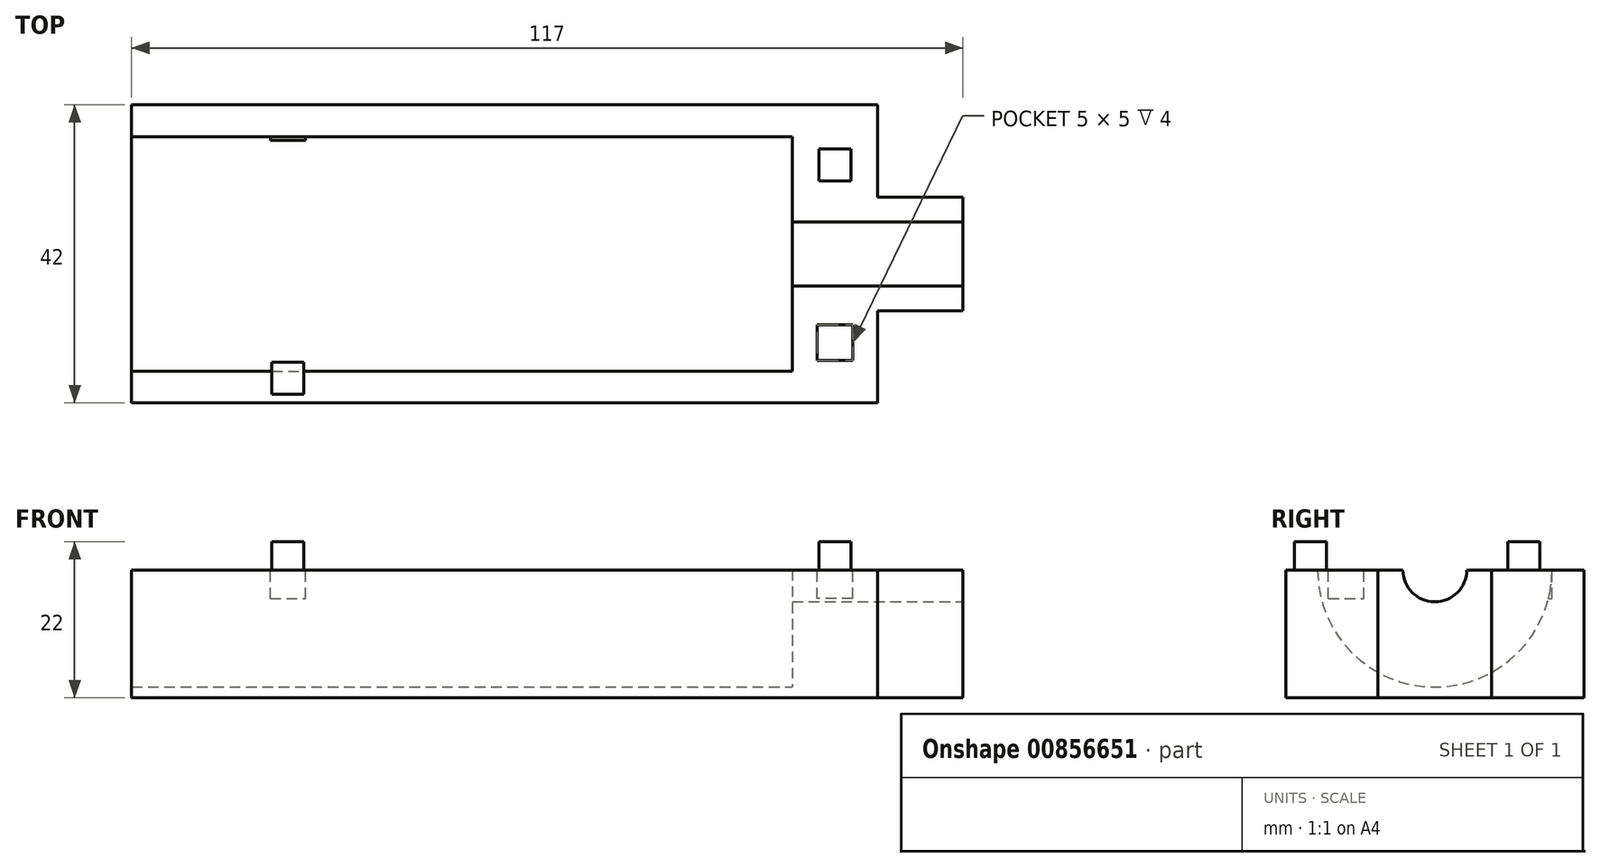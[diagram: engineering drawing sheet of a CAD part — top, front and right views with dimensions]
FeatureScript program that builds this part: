
annotation { "Feature Type Name" : "Feature", "Feature Type Description" : "" }
export const myFeature = defineFeature(function(context is Context, id is Id, definition is map)
    precondition{}
    {
        {
            var Q0;
            Q0=qCreatedBy(makeId("Top.planeOp"),FACE);
            var sketch = newSketch(context, id + "F0", { "sketchPlane" : qUnion([Q0])});
            skLineSegment(sketch, "E0.bottom", {"start": v(40, -21) * mm, "end": v(-40, -21) * mm});
            skLineSegment(sketch, "E0.top", {"start": v(40, 21) * mm, "end": v(-40, 21) * mm});
            skLineSegment(sketch, "E0.left", {"start": v(40, -21) * mm, "end": v(40, 21) * mm});
            skLineSegment(sketch, "E0.right", {"start": v(-40, -21) * mm, "end": v(-40, 21) * mm});
            skPoint(sketch, "E0.middle", {"position": v(0, 0) * mm});
            skSolve(sketch);
        }
        {
            var Q0;
            Q0 = qSketchRegion(id + "F0", true);
            extrude(context, id + "F1", {"entities" : qUnion([Q0]), "depth" : 22 * mm, "offsetDistance" : 25 * mm});
        }
        {
            var Q0;
            Q0=makeQuery(id+"F1.opExtrude","SWEPT_FACE",FACE,{"disambiguationData":[OSD([sQuery(id+"F0.wireOp",EDGE,"E0.left")])]});
            var sketch = newSketch(context, id + "F2", { "sketchPlane" : qUnion([Q0])});
            skCircle(sketch, "E1", {"center": v(0, 22) * mm, "radius": 16.5 * mm});
            skCircle(sketch, "E2", {"center": v(0, 22) * mm, "radius": 14 * mm});
            skCircle(sketch, "E3", {"center": v(0, 22) * mm, "radius": 4.5 * mm});
            skSolve(sketch);
        }
        {
            var Q0;
            {var subQ0=sQuery(id+"F2.wireOp",EDGE,"E1");var subQ1=makeQuery(id+"F1.opExtrude","CAP_EDGE",EDGE,{"disambiguationData":[OSD([sQuery(id+"F0.wireOp",EDGE,"E0.left")])],"isStart":false});var subQ2=makeQuery(id+"F2.imprint","INTERSECT",VERTEX,{"disambiguationData":[OD(0.0)],"derivedFrom":[subQ1,subQ0]});Q0=makeQuery(id+"F2.imprint","IMPRINT",FACE,{"disambiguationData":[TD([[makeQuery(id+"F2.imprint","IMPRINT",EDGE,{"disambiguationData":[TD([[subQ2,-1.0]])],"derivedFrom":subQ0}),1.0]])]});}
            var Q1;
            {var subQ0=sQuery(id+"F2.wireOp",EDGE,"E2");var subQ1=makeQuery(id+"F1.opExtrude","CAP_EDGE",EDGE,{"disambiguationData":[OSD([sQuery(id+"F0.wireOp",EDGE,"E0.left")])],"isStart":false});var subQ2=makeQuery(id+"F2.imprint","INTERSECT",VERTEX,{"disambiguationData":[OD(0.0)],"derivedFrom":[subQ1,subQ0]});Q1=makeQuery(id+"F2.imprint","IMPRINT",FACE,{"disambiguationData":[TD([[makeQuery(id+"F2.imprint","IMPRINT",EDGE,{"disambiguationData":[TD([[subQ2,-1.0]])],"derivedFrom":subQ0}),1.0]])]});}
            var Q2;
            {var subQ0=sQuery(id+"F2.wireOp",EDGE,"E3");var subQ1=makeQuery(id+"F1.opExtrude","CAP_EDGE",EDGE,{"disambiguationData":[OSD([sQuery(id+"F0.wireOp",EDGE,"E0.left")])],"isStart":false});var subQ2=makeQuery(id+"F2.imprint","INTERSECT",VERTEX,{"disambiguationData":[OD(0.0)],"derivedFrom":[subQ1,subQ0]});Q2=makeQuery(id+"F2.imprint","IMPRINT",FACE,{"disambiguationData":[TD([[makeQuery(id+"F2.imprint","IMPRINT",EDGE,{"disambiguationData":[TD([[subQ2,-1.0]])],"derivedFrom":subQ0}),1.0]])]});}
            extrude(context, id + "F3", {"entities" : qUnion([Q0, Q1, Q2]), "operationType" : NewBodyOperationType.REMOVE, "oppositeDirection" : true, "depth" : 80 * mm, "offsetDistance" : 25 * mm});
        }
        {
            var Q0;
            {var subQ0=sQuery(id+"F2.wireOp",EDGE,"E1");var subQ1=makeQuery(id+"F1.opExtrude","CAP_EDGE",EDGE,{"disambiguationData":[OSD([sQuery(id+"F0.wireOp",EDGE,"E0.left")])],"isStart":false});var subQ2=makeQuery(id+"F2.imprint","INTERSECT",VERTEX,{"disambiguationData":[OD(0.0)],"derivedFrom":[subQ1,subQ0]});Q0=makeQuery(id+"F2.imprint","IMPRINT",FACE,{"disambiguationData":[TD([[makeQuery(id+"F2.imprint","IMPRINT",EDGE,{"disambiguationData":[TD([[subQ2,-1.0]])],"derivedFrom":subQ0}),1.0]])]});}
            extrude(context, id + "F4", {"entities" : qUnion([Q0]), "operationType" : NewBodyOperationType.ADD, "oppositeDirection" : true, "depth" : 2 * mm, "offsetDistance" : 25 * mm});
        }
        {
            var Q0;
            Q0=makeQuery(id+"F1.opExtrude","SWEPT_FACE",FACE,{"disambiguationData":[OSD([sQuery(id+"F0.wireOp",EDGE,"E0.right")])]});
            var sketch = newSketch(context, id + "F5", { "sketchPlane" : qUnion([Q0])});
            skCircle(sketch, "E4", {"center": v(0, 22) * mm, "radius": 14 * mm});
            skLineSegment(sketch, "E5", {"start": v(-16.5, 22) * mm, "end": v(16.5, 22) * mm});
            skSolve(sketch);
        }
        {
            var Q0;
            {var subQ0=sQuery(id+"F5.wireOp",EDGE,"E5");var subQ1=sQuery(id+"F5.wireOp",EDGE,"E4");var subQ2=makeQuery(id+"F5.imprint","INTERSECT",VERTEX,{"disambiguationData":[OD(0.0)],"derivedFrom":[subQ1,subQ0]});Q0=makeQuery(id+"F5.imprint","IMPRINT",FACE,{"disambiguationData":[TD([[makeQuery(id+"F5.imprint","IMPRINT",EDGE,{"disambiguationData":[TD([[subQ2,-1.0]])],"derivedFrom":subQ1}),1.0]])]});}
            var Q1;
            {var subQ8=sQuery(id+"F2.wireOp",EDGE,"E1");var subQ12=makeQuery(id+"F3.boolean.opBoolean","COPY",EDGE,{"derivedFrom":makeQuery(id+"F3.opExtrude","CAP_EDGE",EDGE,{"disambiguationData":[OSD([subQ8])],"isStart":false})});Q1=makeQuery(id+"F5.imprint","IMPRINT",FACE,{"disambiguationData":[TD([[makeQuery(id+"F5.imprint","IMPRINT",EDGE,{"derivedFrom":subQ12}),-1.0]])]});}
            extrude(context, id + "F6", {"entities" : qUnion([Q0, Q1]), "operationType" : NewBodyOperationType.ADD, "oppositeDirection" : true, "depth" : 22 * mm, "offsetDistance" : 25 * mm});
        }
        {
            var Q0;
            {var subQ0=sQuery(id+"F5.wireOp",EDGE,"E5");var subQ1=sQuery(id+"F5.wireOp",EDGE,"E4");var subQ2=makeQuery(id+"F5.imprint","INTERSECT",VERTEX,{"disambiguationData":[OD(0.0)],"derivedFrom":[subQ1,subQ0]});Q0=makeQuery(id+"F5.imprint","IMPRINT",FACE,{"disambiguationData":[TD([[makeQuery(id+"F5.imprint","IMPRINT",EDGE,{"disambiguationData":[TD([[subQ2,-1.0]])],"derivedFrom":subQ1}),1.0]])]});}
            extrude(context, id + "F7", {"entities" : qUnion([Q0]), "operationType" : NewBodyOperationType.REMOVE, "oppositeDirection" : true, "depth" : 28 * mm, "offsetDistance" : 25 * mm});
        }
        {
            var Q0;
            Q0=makeQuery(id+"F6.boolean.opBoolean","MERGE",FACE,{"derivedFrom":[makeQuery(id+"F1.opExtrude","SWEPT_FACE",FACE,{"disambiguationData":[OSD([sQuery(id+"F0.wireOp",EDGE,"E0.right")])]}),makeQuery(id+"F6.opExtrude","CAP_FACE",FACE,{"disambiguationData":[OSD([sQuery(id+"F2.wireOp",EDGE,"E1"),sQuery(id+"F5.wireOp",EDGE,"E5")])],"isStart":true})]});
            extrude(context, id + "F8", {"entities" : qUnion([Q0]), "operationType" : NewBodyOperationType.ADD, "depth" : 15 * mm, "offsetDistance" : 25 * mm});
        }
        {
            var Q0;
            {var subQ0=sQuery(id+"F2.wireOp",EDGE,"E2");var subQ1=makeQuery(id+"F1.opExtrude","CAP_EDGE",EDGE,{"disambiguationData":[OSD([sQuery(id+"F0.wireOp",EDGE,"E0.left")])],"isStart":false});var subQ2=makeQuery(id+"F2.imprint","INTERSECT",VERTEX,{"disambiguationData":[OD(0.0)],"derivedFrom":[subQ1,subQ0]});Q0=makeQuery(id+"F2.imprint","IMPRINT",FACE,{"disambiguationData":[TD([[makeQuery(id+"F2.imprint","IMPRINT",EDGE,{"disambiguationData":[TD([[subQ2,-1.0]])],"derivedFrom":subQ0}),1.0]])]});}
            extrude(context, id + "F9", {"entities" : qUnion([Q0]), "operationType" : NewBodyOperationType.ADD, "oppositeDirection" : true, "depth" : 2 * mm, "offsetDistance" : 25 * mm});
        }
        {
            var Q0;
            {var subQ0=sQuery(id+"F2.wireOp",EDGE,"E2");var subQ1=sQuery(id+"F0.wireOp",EDGE,"E0.left");Q0=makeQuery(id+"F9.boolean.opBoolean","MERGE",FACE,{"derivedFrom":[makeQuery(id+"F4.boolean.opBoolean","MERGE",FACE,{"derivedFrom":[makeQuery(id+"F1.opExtrude","SWEPT_FACE",FACE,{"disambiguationData":[OSD([subQ1])]}),makeQuery(id+"F4.opExtrude","CAP_FACE",FACE,{"disambiguationData":[OSD([subQ1,sQuery(id+"F2.wireOp",EDGE,"E1"),subQ0])],"isStart":true})]}),makeQuery(id+"F9.opExtrude","CAP_FACE",FACE,{"disambiguationData":[OSD([subQ1,subQ0,sQuery(id+"F2.wireOp",EDGE,"E3")])],"isStart":true})]});}
            extrude(context, id + "F10", {"entities" : qUnion([Q0]), "operationType" : NewBodyOperationType.ADD, "depth" : 10 * mm, "offsetDistance" : 25 * mm});
        }
        {
            var Q0;
            {var subQ0=sQuery(id+"F2.wireOp",EDGE,"E2");var subQ1=sQuery(id+"F0.wireOp",EDGE,"E0.left");var subQ2=makeQuery(id+"F1.opExtrude","CAP_EDGE",EDGE,{"disambiguationData":[OSD([subQ1])],"isStart":false});var subQ3=makeQuery(id+"F2.imprint","INTERSECT",VERTEX,{"disambiguationData":[OD(1.0)],"derivedFrom":[subQ2,subQ0]});var subQ4=makeQuery(id+"F2.imprint","IMPRINT",EDGE,{"disambiguationData":[TD([[subQ3,1.0]])],"derivedFrom":subQ2});var subQ5=sQuery(id+"F2.wireOp",EDGE,"E1");var subQ6=makeQuery(id+"F2.imprint","IMPRINT",EDGE,{"disambiguationData":[TD([[makeQuery(id+"F2.imprint","INTERSECT",VERTEX,{"disambiguationData":[OD(1.0)],"derivedFrom":[subQ2,subQ5]}),1.0]])],"derivedFrom":subQ2});var subQ7=sQuery(id+"F0.wireOp",EDGE,"E0.right");var subQ8=sQuery(id+"F0.wireOp",EDGE,"E0.top");var subQ9=sQuery(id+"F0.wireOp",EDGE,"E0.bottom");var subQ10=makeQuery(id+"F1.opExtrude","CAP_FACE",FACE,{"disambiguationData":[OSD([subQ9,subQ8,subQ1,subQ7])],"isStart":false});var subQ11=makeQuery(id+"F1.opExtrude","SWEPT_FACE",FACE,{"disambiguationData":[OSD([subQ8])]});var subQ14=makeQuery(id+"F4.opExtrude","SWEPT_FACE",FACE,{"disambiguationData":[OSD([subQ1]),TDD([makeQuery(id+"F2.imprint","IMPRINT",EDGE,{"disambiguationData":[TD([[makeQuery(id+"F2.imprint","INTERSECT",VERTEX,{"disambiguationData":[OD(0.0)],"derivedFrom":[subQ2,subQ5]}),-1.0]])],"derivedFrom":subQ2})])]});var subQ16=makeQuery(id+"F4.opExtrude","SWEPT_FACE",FACE,{"disambiguationData":[OSD([subQ1]),TDD([subQ6])]});var subQ17=sQuery(id+"F5.wireOp",EDGE,"E5");var subQ18=makeQuery(id+"F6.opExtrude","SWEPT_FACE",FACE,{"disambiguationData":[OSD([subQ17])]});var subQ21=makeQuery(id+"F1.opExtrude","CAP_EDGE",EDGE,{"disambiguationData":[OSD([subQ7])],"isStart":false});var subQ22=makeQuery(id+"F1.opExtrude","SWEPT_FACE",FACE,{"disambiguationData":[OSD([subQ9])]});Q0=makeQuery(id+"F10.boolean.opBoolean","MERGE",FACE,{"derivedFrom":[makeQuery(id+"F9.boolean.opBoolean","MERGE",FACE,{"derivedFrom":[makeQuery(id+"F8.boolean.opBoolean","MERGE",FACE,{"derivedFrom":[makeQuery(id+"F7.boolean.opBoolean","SPLIT",FACE,{"disambiguationData":[TD([subQ11])],"derivedFrom":makeQuery(id+"F6.boolean.opBoolean","MERGE",FACE,{"derivedFrom":[makeQuery(id+"F4.boolean.opBoolean","MERGE",FACE,{"derivedFrom":[makeQuery(id+"F3.boolean.opBoolean","SPLIT",FACE,{"disambiguationData":[TD([subQ22])],"derivedFrom":subQ10}),subQ14]}),makeQuery(id+"F4.boolean.opBoolean","MERGE",FACE,{"derivedFrom":[makeQuery(id+"F3.boolean.opBoolean","SPLIT",FACE,{"disambiguationData":[TD([subQ11])],"derivedFrom":subQ10}),subQ16]}),subQ18]})}),makeQuery(id+"F8.opExtrude","SWEPT_FACE",FACE,{"disambiguationData":[OSD([subQ7,subQ17]),TDD([makeQuery(id+"F7.boolean.opBoolean","SPLIT",EDGE,{"disambiguationData":[TD([subQ11])],"derivedFrom":makeQuery(id+"F6.boolean.opBoolean","MERGE",EDGE,{"derivedFrom":[makeQuery(id+"F3.boolean.opBoolean","SPLIT",EDGE,{"disambiguationData":[TD([subQ22])],"derivedFrom":subQ21}),makeQuery(id+"F3.boolean.opBoolean","SPLIT",EDGE,{"disambiguationData":[TD([subQ11])],"derivedFrom":subQ21}),makeQuery(id+"F6.opExtrude","CAP_EDGE",EDGE,{"disambiguationData":[OSD([subQ17])],"isStart":true})]})})])]})]}),makeQuery(id+"F9.opExtrude","SWEPT_FACE",FACE,{"disambiguationData":[OSD([subQ1]),TDD([subQ4])]})]}),makeQuery(id+"F10.opExtrude","SWEPT_FACE",FACE,{"disambiguationData":[OSD([subQ1]),TDD([makeQuery(id+"F9.boolean.opBoolean","MERGE",EDGE,{"derivedFrom":[makeQuery(id+"F4.boolean.opBoolean","MERGE",EDGE,{"derivedFrom":[makeQuery(id+"F3.boolean.opBoolean","SPLIT",EDGE,{"disambiguationData":[TD([subQ11])],"derivedFrom":subQ2}),makeQuery(id+"F4.opExtrude","CAP_EDGE",EDGE,{"disambiguationData":[OSD([subQ1]),TDD([subQ6])],"isStart":true})]}),makeQuery(id+"F9.opExtrude","CAP_EDGE",EDGE,{"disambiguationData":[OSD([subQ1]),TDD([subQ4])],"isStart":true})]})])]})]});}
            var sketch = newSketch(context, id + "F11", { "sketchPlane" : qUnion([Q0])});
            skLineSegment(sketch, "E6.bottom", {"start": v(-36.5, 14) * mm, "end": v(-29.5, 14) * mm});
            skLineSegment(sketch, "E6.top", {"start": v(-36.5, 21) * mm, "end": v(-29.5, 21) * mm});
            skLineSegment(sketch, "E6.left", {"start": v(-36.5, 14) * mm, "end": v(-36.5, 21) * mm});
            skLineSegment(sketch, "E6.right", {"start": v(-29.5, 14) * mm, "end": v(-29.5, 21) * mm});
            skLineSegment(sketch, "E7.bottom", {"start": v(-30.5, 15) * mm, "end": v(-35.5, 15) * mm});
            skLineSegment(sketch, "E7.top", {"start": v(-30.5, 20) * mm, "end": v(-35.5, 20) * mm});
            skLineSegment(sketch, "E7.left", {"start": v(-30.5, 15) * mm, "end": v(-30.5, 20) * mm});
            skLineSegment(sketch, "E7.right", {"start": v(-35.5, 15) * mm, "end": v(-35.5, 20) * mm});
            skPoint(sketch, "E7.middle", {"position": v(-33, 17.5) * mm});
            skPoint(sketch, "E7.middle.positionSnap0", {"position": v(-29.5, 17.5) * mm});
            skPoint(sketch, "E7.middle.positionSnap1", {"position": v(-33, 21) * mm});
            skPoint(sketch, "E7.centerSnap0", {"position": v(-29.5, 17.5) * mm});
            skPoint(sketch, "E7.centerSnap1", {"position": v(-33, 21) * mm});
            skPoint(sketch, "E8.MirrorP", {"position": v(-33, -21) * mm});
            skPoint(sketch, "E9.MirrorP", {"position": v(-29.5, -17.5) * mm});
            skLineSegment(sketch, "E10.MirrorCS", {"start": v(-36.5, -14) * mm, "end": v(-29.5, -14) * mm});
            skLineSegment(sketch, "E11.MirrorCS", {"start": v(-36.5, -14) * mm, "end": v(-36.5, -21) * mm});
            skLineSegment(sketch, "E12.MirrorCS", {"start": v(-36.5, -21) * mm, "end": v(-29.5, -21) * mm});
            skPoint(sketch, "E13.MirrorP", {"position": v(-33, -17.5) * mm});
            skLineSegment(sketch, "E14.MirrorCS", {"start": v(-29.5, -14) * mm, "end": v(-29.5, -21) * mm});
            skLineSegment(sketch, "E15.bottom", {"start": v(-30.75, -19.75) * mm, "end": v(-35.25, -19.75) * mm});
            skLineSegment(sketch, "E15.top", {"start": v(-30.75, -15.25) * mm, "end": v(-35.25, -15.25) * mm});
            skLineSegment(sketch, "E15.left", {"start": v(-30.75, -19.75) * mm, "end": v(-30.75, -15.25) * mm});
            skLineSegment(sketch, "E15.right", {"start": v(-35.25, -19.75) * mm, "end": v(-35.25, -15.25) * mm});
            skLineSegment(sketch, "E16.bottom", {"start": v(46.25, 10.25) * mm, "end": v(41.75, 10.25) * mm});
            skLineSegment(sketch, "E16.top", {"start": v(46.25, 14.75) * mm, "end": v(41.75, 14.75) * mm});
            skLineSegment(sketch, "E16.left", {"start": v(46.25, 10.25) * mm, "end": v(46.25, 14.75) * mm});
            skLineSegment(sketch, "E16.right", {"start": v(41.75, 10.25) * mm, "end": v(41.75, 14.75) * mm});
            skPoint(sketch, "E16.middle", {"position": v(44, 12.5) * mm});
            skPoint(sketch, "E16.middle.positionSnap0", {"position": v(44, 4.5) * mm});
            skPoint(sketch, "E16.centerSnap0", {"position": v(44, 4.5) * mm});
            skLineSegment(sketch, "E17.bottom", {"start": v(46.5, -15) * mm, "end": v(41.5, -15) * mm});
            skLineSegment(sketch, "E17.top", {"start": v(46.5, -10) * mm, "end": v(41.5, -10) * mm});
            skLineSegment(sketch, "E17.left", {"start": v(46.5, -15) * mm, "end": v(46.5, -10) * mm});
            skLineSegment(sketch, "E17.right", {"start": v(41.5, -15) * mm, "end": v(41.5, -10) * mm});
            skPoint(sketch, "E17.middle", {"position": v(44, -12.5) * mm});
            skSolve(sketch);
        }
        {
            var Q0;
            Q0=makeQuery(id+"F11.imprint","IMPRINT",FACE,{"disambiguationData":[TD([[makeQuery(id+"F11.imprint","IMPRINT",EDGE,{"derivedFrom":sQuery(id+"F11.wireOp",EDGE,"E7.bottom")}),-1.0]])]});
            var Q1;
            Q1=makeQuery(id+"F11.imprint","IMPRINT",FACE,{"disambiguationData":[TD([[makeQuery(id+"F11.imprint","IMPRINT",EDGE,{"derivedFrom":sQuery(id+"F11.wireOp",EDGE,"y81X3ZTq-tmHN-0zrA-wdGu-nb1mPW9eMlfj.bottom")}),-1.0]])]});
            var Q2;
            Q2=makeQuery(id+"F11.imprint","IMPRINT",FACE,{"disambiguationData":[TD([[makeQuery(id+"F11.imprint","IMPRINT",EDGE,{"derivedFrom":sQuery(id+"F11.wireOp",EDGE,"E17.bottom")}),-1.0]])]});
            extrude(context, id + "F12", {"entities" : qUnion([Q0, Q1, Q2]), "operationType" : NewBodyOperationType.REMOVE, "oppositeDirection" : true, "depth" : 4 * mm, "offsetDistance" : 25 * mm});
        }
        {
            var Q0;
            Q0=makeQuery(id+"F11.imprint","IMPRINT",FACE,{"disambiguationData":[TD([[makeQuery(id+"F11.imprint","IMPRINT",EDGE,{"derivedFrom":sQuery(id+"F11.wireOp",EDGE,"E15.bottom")}),-1.0]])]});
            var Q1;
            Q1=makeQuery(id+"F11.imprint","IMPRINT",FACE,{"disambiguationData":[TD([[makeQuery(id+"F11.imprint","IMPRINT",EDGE,{"derivedFrom":sQuery(id+"F11.wireOp",EDGE,"E16.bottom")}),-1.0]])]});
            extrude(context, id + "F13", {"entities" : qUnion([Q0, Q1]), "operationType" : NewBodyOperationType.ADD, "depth" : 4 * mm, "offsetDistance" : 25 * mm});
        }
        {
            var Q0;
            Q0=makeQuery(id+"F10.opExtrude","CAP_FACE",FACE,{"disambiguationData":[OSD([sQuery(id+"F0.wireOp",EDGE,"E0.left"),sQuery(id+"F2.wireOp",EDGE,"E1"),sQuery(id+"F2.wireOp",EDGE,"E2"),sQuery(id+"F2.wireOp",EDGE,"E3")])],"isStart":false});
            extrude(context, id + "F14", {"entities" : qUnion([Q0]), "operationType" : NewBodyOperationType.ADD, "depth" : 12 * mm, "offsetDistance" : 25 * mm});
        }
        {
            var Q0;
            {var subQ0=sQuery(id+"F0.wireOp",EDGE,"E0.left");var subQ1=makeQuery(id+"F1.opExtrude","CAP_EDGE",EDGE,{"disambiguationData":[OSD([subQ0])],"isStart":true});var subQ2=sQuery(id+"F0.wireOp",EDGE,"E0.right");Q0=makeQuery(id+"F14.boolean.opBoolean","MERGE",FACE,{"derivedFrom":[makeQuery(id+"F10.boolean.opBoolean","MERGE",FACE,{"derivedFrom":[makeQuery(id+"F8.boolean.opBoolean","MERGE",FACE,{"derivedFrom":[makeQuery(id+"F1.opExtrude","CAP_FACE",FACE,{"disambiguationData":[OSD([sQuery(id+"F0.wireOp",EDGE,"E0.bottom"),sQuery(id+"F0.wireOp",EDGE,"E0.top"),subQ0,subQ2])],"isStart":true}),makeQuery(id+"F8.opExtrude","SWEPT_FACE",FACE,{"disambiguationData":[OSD([subQ2])]})]}),makeQuery(id+"F10.opExtrude","SWEPT_FACE",FACE,{"disambiguationData":[OSD([subQ0]),TDD([subQ1])]})]}),makeQuery(id+"F14.opExtrude","SWEPT_FACE",FACE,{"disambiguationData":[OSD([subQ0]),TDD([makeQuery(id+"F10.opExtrude","CAP_EDGE",EDGE,{"disambiguationData":[OSD([subQ0]),TDD([subQ1])],"isStart":false})])]})]});}
            extrude(context, id + "F15", {"entities" : qUnion([Q0]), "operationType" : NewBodyOperationType.REMOVE, "oppositeDirection" : true, "depth" : 4 * mm, "offsetDistance" : 25 * mm});
        }
        {
            var Q0;
            Q0=makeQuery(id+"F14.opExtrude","CAP_FACE",FACE,{"disambiguationData":[OSD([sQuery(id+"F0.wireOp",EDGE,"E0.left"),sQuery(id+"F2.wireOp",EDGE,"E1"),sQuery(id+"F2.wireOp",EDGE,"E2"),sQuery(id+"F2.wireOp",EDGE,"E3")])],"isStart":false});
            var sketch = newSketch(context, id + "F16", { "sketchPlane" : qUnion([Q0])});
            skLineSegment(sketch, "E18", {"start": v(-8, 22) * mm, "end": v(-8, 4) * mm});
            skLineSegment(sketch, "E19.MirrorCS", {"start": v(8, 22) * mm, "end": v(8, 4) * mm});
            skSolve(sketch);
        }
        {
            var Q0;
            {var subQ0=sQuery(id+"F16.wireOp",EDGE,"E18");Q0=makeQuery(id+"F16.imprint","IMPRINT",FACE,{"disambiguationData":[TD([[makeQuery(id+"F16.imprint","IMPRINT",EDGE,{"derivedFrom":subQ0}),-1.0]])]});}
            var Q1;
            {var subQ0=sQuery(id+"F16.wireOp",EDGE,"E19.MirrorCS");Q1=makeQuery(id+"F16.imprint","IMPRINT",FACE,{"disambiguationData":[TD([[makeQuery(id+"F16.imprint","IMPRINT",EDGE,{"derivedFrom":subQ0}),1.0]])]});}
            extrude(context, id + "F17", {"entities" : qUnion([Q0, Q1]), "operationType" : NewBodyOperationType.REMOVE, "oppositeDirection" : true, "depth" : 12 * mm, "offsetDistance" : 25 * mm});
        }
    });
